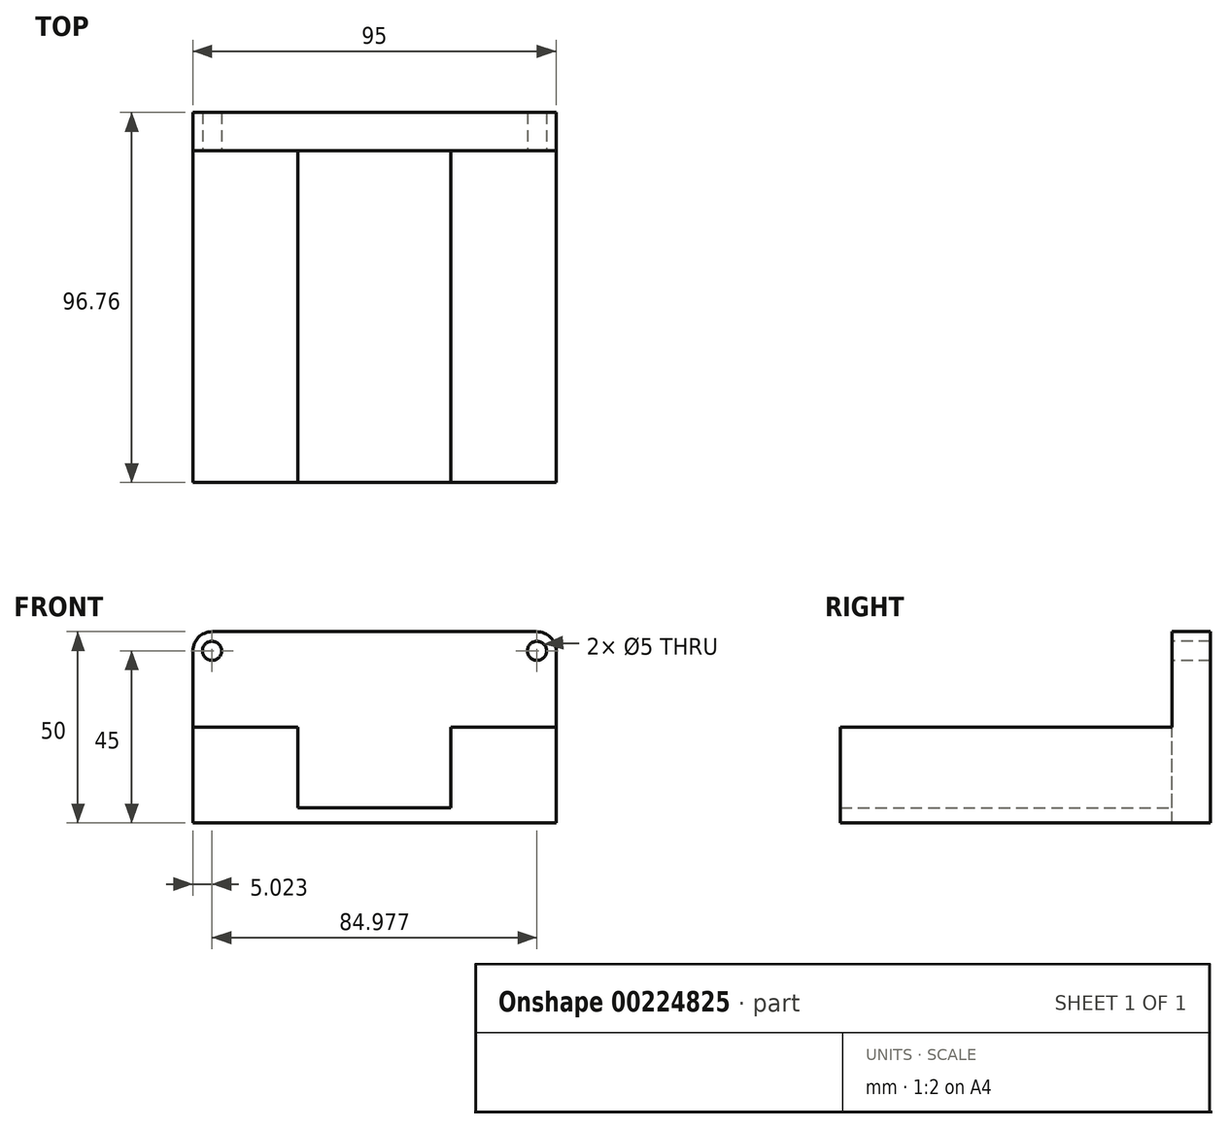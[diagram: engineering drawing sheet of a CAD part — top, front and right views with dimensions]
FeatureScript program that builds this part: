
annotation { "Feature Type Name" : "Feature", "Feature Type Description" : "" }
export const myFeature = defineFeature(function(context is Context, id is Id, definition is map)
    precondition{}
    {
        {
            var Q0;
            Q0=qCreatedBy(makeId("Top.planeOp"),FACE);
            var sketch = newSketch(context, id + "F0", { "sketchPlane" : qUnion([Q0])});
            skLineSegment(sketch, "E0.bottom", {"start": v(-20, -43.38) * mm, "end": v(20, -43.38) * mm});
            skLineSegment(sketch, "E0.top", {"start": v(-20, 43.38) * mm, "end": v(20, 43.38) * mm});
            skLineSegment(sketch, "E0.left", {"start": v(-20, -43.38) * mm, "end": v(-20, 43.38) * mm});
            skLineSegment(sketch, "E0.right", {"start": v(20, -43.38) * mm, "end": v(20, 43.38) * mm});
            skPoint(sketch, "E0.middle", {"position": v(0, 0) * mm});
            skSolve(sketch);
        }
        {
            var Q0;
            Q0=makeQuery(id+"F0.imprint","IMPRINT",FACE,{"disambiguationData":[TD([[makeQuery(id+"F0.imprint","IMPRINT",EDGE,{"derivedFrom":sQuery(id+"F0.wireOp",EDGE,"E0.bottom")}),1.0]])]});
            extrude(context, id + "F1", {"entities" : qUnion([Q0]), "depth" : 4 * mm});
        }
        {
            var Q0;
            Q0=makeQuery(id+"F1.opExtrude","SWEPT_FACE",FACE,{"disambiguationData":[OSD([sQuery(id+"F0.wireOp",EDGE,"E0.right")])]});
            var sketch = newSketch(context, id + "F2", { "sketchPlane" : qUnion([Q0])});
            skLineSegment(sketch, "E1.bottom", {"start": v(-43.38, 0) * mm, "end": v(51.62, 0) * mm});
            skLineSegment(sketch, "E1.top", {"start": v(-43.38, 25) * mm, "end": v(51.62, 25) * mm});
            skLineSegment(sketch, "E1.left", {"start": v(-43.38, 0) * mm, "end": v(-43.38, 25) * mm});
            skLineSegment(sketch, "E1.right", {"start": v(51.62, 0) * mm, "end": v(51.62, 25) * mm});
            skSolve(sketch);
        }
        {
            var Q0;
            Q0=qSketchRegion(id+"F2",true);
            extrude(context, id + "F3", {"entities" : qUnion([Q0]), "operationType" : NewBodyOperationType.ADD, "depth" : 27.5 * mm});
        }
        {
            var Q0;
            Q0=makeQuery(id+"F1.opExtrude","SWEPT_FACE",FACE,{"disambiguationData":[OSD([sQuery(id+"F0.wireOp",EDGE,"E0.left")])]});
            var sketch = newSketch(context, id + "F4", { "sketchPlane" : qUnion([Q0])});
            skLineSegment(sketch, "E2.bottom", {"start": v(-43.38, 0) * mm, "end": v(43.38, 0) * mm});
            skLineSegment(sketch, "E2.top", {"start": v(-43.38, 25) * mm, "end": v(43.38, 25) * mm});
            skLineSegment(sketch, "E2.left", {"start": v(-43.38, 0) * mm, "end": v(-43.38, 25) * mm});
            skLineSegment(sketch, "E2.right", {"start": v(43.38, 0) * mm, "end": v(43.38, 25) * mm});
            skSolve(sketch);
        }
        {
            var Q0;
            Q0=qSketchRegion(id+"F4",true);
            extrude(context, id + "F5", {"entities" : qUnion([Q0]), "operationType" : NewBodyOperationType.ADD, "depth" : 27.5 * mm});
        }
        {
            var Q0;
            Q0=makeQuery(id+"F5.boolean.opBoolean","MERGE",FACE,{"derivedFrom":[makeQuery(id+"F3.boolean.opBoolean","MERGE",FACE,{"derivedFrom":[makeQuery(id+"F1.opExtrude","SWEPT_FACE",FACE,{"disambiguationData":[OSD([sQuery(id+"F0.wireOp",EDGE,"E0.top")])]}),makeQuery(id+"F3.opExtrude","SWEPT_FACE",FACE,{"disambiguationData":[OSD([sQuery(id+"F2.wireOp",EDGE,"E1.right")])]})]}),makeQuery(id+"F5.opExtrude","SWEPT_FACE",FACE,{"disambiguationData":[OSD([sQuery(id+"F4.wireOp",EDGE,"E2.left")])]})]});
            var sketch = newSketch(context, id + "F6", { "sketchPlane" : qUnion([Q0])});
            skLineSegment(sketch, "E3.bottom", {"start": v(-47.5, 0) * mm, "end": v(47.48, 0) * mm});
            skLineSegment(sketch, "E3.top", {"start": v(-47.5, 50) * mm, "end": v(47.48, 50) * mm});
            skLineSegment(sketch, "E3.left", {"start": v(-47.5, 0) * mm, "end": v(-47.5, 50) * mm});
            skLineSegment(sketch, "E3.right", {"start": v(47.48, 0) * mm, "end": v(47.48, 50) * mm});
            skSolve(sketch);
        }
        {
            var Q0;
            Q0=qSketchRegion(id+"F6",true);
            extrude(context, id + "F7", {"entities" : qUnion([Q0]), "operationType" : NewBodyOperationType.ADD, "depth" : 10 * mm});
        }
        {
            var Q0;
            Q0=makeQuery(id+"F7.opExtrude","SWEPT_EDGE",EDGE,{"disambiguationData":[OSD([sQuery(id+"F6.wireOp",EDGE,"E3.top"),sQuery(id+"F6.wireOp",EDGE,"E3.left")])]});
            fillet(context, id + "F8", {"entities" : qUnion([Q0]), "radius" : 5 * mm, "tangentPropagation" : true, "allowEdgeOverflow" : false});
        }
        {
            var Q0;
            Q0=makeQuery(id+"F7.opExtrude","SWEPT_EDGE",EDGE,{"disambiguationData":[OSD([sQuery(id+"F6.wireOp",EDGE,"E3.top"),sQuery(id+"F6.wireOp",EDGE,"E3.right")])]});
            fillet(context, id + "F9", {"entities" : qUnion([Q0]), "radius" : 5 * mm, "tangentPropagation" : true, "allowEdgeOverflow" : false});
        }
        {
            var Q0;
            Q0=makeQuery(id+"F7.opExtrude","CAP_FACE",FACE,{"disambiguationData":[OSD([sQuery(id+"F6.wireOp",EDGE,"E3.bottom"),sQuery(id+"F6.wireOp",EDGE,"E3.top"),sQuery(id+"F6.wireOp",EDGE,"E3.left"),sQuery(id+"F6.wireOp",EDGE,"E3.right")])],"isStart":true});
            var sketch = newSketch(context, id + "F10", { "sketchPlane" : qUnion([Q0])});
            skCircle(sketch, "E4", {"center": v(-42.48, 45) * mm, "radius": 2.5 * mm});
            skCircle(sketch, "E5", {"center": v(42.5, 45) * mm, "radius": 2.5 * mm});
            skSolve(sketch);
        }
        {
            var Q0;
            Q0=qSketchRegion(id+"F10",true);
            extrude(context, id + "F11", {"entities" : qUnion([Q0]), "operationType" : NewBodyOperationType.REMOVE, "endBound" : BoundingType.THROUGH_ALL, "oppositeDirection" : true, "depth" : 25 * mm});
        }
    });
